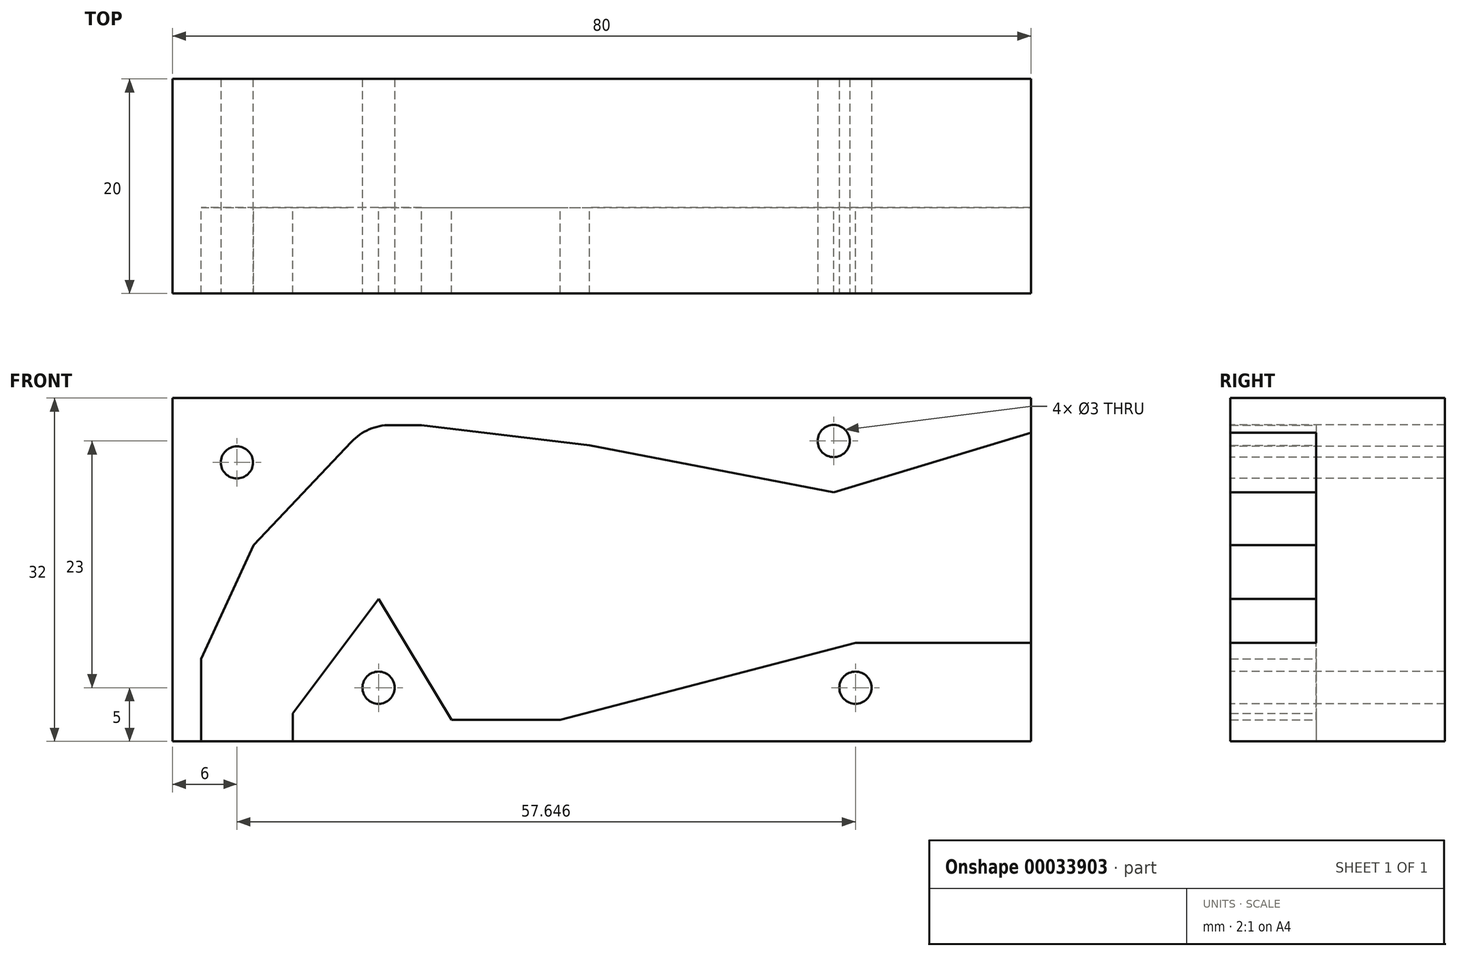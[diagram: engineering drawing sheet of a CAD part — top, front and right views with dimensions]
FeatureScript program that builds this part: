
annotation { "Feature Type Name" : "Feature", "Feature Type Description" : "" }
export const myFeature = defineFeature(function(context is Context, id is Id, definition is map)
    precondition{}
    {
        {
            var Q0;
            Q0=qCreatedBy(makeId("Front.planeOp"),FACE);
            var sketch = newSketch(context, id + "F0", { "sketchPlane" : qUnion([Q0])});
            skCircle(sketch, "E0", {"center": v(0, 0) * mm, "radius": 8 * mm});
            skLineSegment(sketch, "E1", {"start": v(0, 0) * mm, "end": v(0, 12.66) * mm});
            skArc(sketch, "E2", {"start": v(-7.6, 13.48) * mm, "mid": v(-0.91, 8.05) * mm, "end": v(6.83, 11.83) * mm});
            skLineSegment(sketch, "E3", {"start": v(0, 0) * mm, "end": v(0, -16) * mm});
            skLineSegment(sketch, "E4", {"start": v(0, 0) * mm, "end": v(8, 0) * mm});
            skPoint(sketch, "E5.endSnap0", {"position": v(0, -8) * mm});
            skLineSegment(sketch, "E6", {"start": v(-3.6, 8.53) * mm, "end": v(-19.6, -12.8) * mm});
            skLineSegment(sketch, "E7.top", {"start": v(-30, 16) * mm, "end": v(50, 16) * mm});
            skLineSegment(sketch, "E7.left", {"start": v(-30, -16) * mm, "end": v(-30, 16) * mm});
            skCircle(sketch, "E8", {"center": v(-22.8, -10.4) * mm, "radius": 4 * mm});
            skLineSegment(sketch, "E9", {"start": v(-26.25, -8.34) * mm, "end": v(-19.35, 0.86) * mm});
            skLineSegment(sketch, "E10", {"start": v(-8, 13.48) * mm, "end": v(-8, 0) * mm});
            skLineSegment(sketch, "E11", {"start": v(-8, 12.14) * mm, "end": v(-19.17, -12.08) * mm});
            skLineSegment(sketch, "E12", {"start": v(-26.43, -8.72) * mm, "end": v(-19.17, -12.08) * mm});
            skLineSegment(sketch, "E13", {"start": v(-26.43, -8.72) * mm, "end": v(-21.62, 1.72) * mm});
            skArc(sketch, "E14", {"start": v(-3.6, 8.53) * mm, "mid": v(-5.94, 9.33) * mm, "end": v(-8.3, 8.6) * mm});
            skArc(sketch, "E15.trimOffspring", {"start": v(0.36, 8) * mm, "mid": v(0.36, 8) * mm, "end": v(0.37, 8) * mm});
            skArc(sketch, "E16.trimOffspring", {"start": v(-6, 5.33) * mm, "mid": v(-5.99, 5.33) * mm, "end": v(-5.98, 5.32) * mm});
            skArc(sketch, "E17.trimOffspring", {"start": v(-7.83, 12.02) * mm, "mid": v(-10.35, 12.43) * mm, "end": v(-12.6, 11.23) * mm});
            skArc(sketch, "E18.trimOffspring", {"start": v(-8, 12.14) * mm, "mid": v(-9.1, 12.82) * mm, "end": v(-10.23, 13.45) * mm});
            skLineSegment(sketch, "E19", {"start": v(-21.62, 1.72) * mm, "end": v(-12.6, 11.23) * mm});
            skLineSegment(sketch, "E20", {"start": v(-19.35, 0.86) * mm, "end": v(-8, 8.82) * mm});
            skLineSegment(sketch, "E21.0", {"start": v(-27.34, -8.3) * mm, "end": v(-22.46, 2.29) * mm});
            skLineSegment(sketch, "E22.0", {"start": v(-22.46, 2.29) * mm, "end": v(-13.33, 11.92) * mm});
            skArc(sketch, "E23.0", {"start": v(-7.37, 12.9) * mm, "mid": v(-7.37, 12.9) * mm, "end": v(-7.38, 12.91) * mm});
            skLineSegment(sketch, "E24", {"start": v(-8, 13.48) * mm, "end": v(-9.7, 13.48) * mm});
            skArc(sketch, "E25.trimOffspring", {"start": v(-9.7, 13.48) * mm, "mid": v(-11.67, 13.08) * mm, "end": v(-13.33, 11.92) * mm});
            skLineSegment(sketch, "E26", {"start": v(-27.34, -8.3) * mm, "end": v(-27.34, -16) * mm});
            skLineSegment(sketch, "E27.0", {"start": v(-7.92, 1.1) * mm, "end": v(-8, 1) * mm});
            skLineSegment(sketch, "E28", {"start": v(-18.8, -13.4) * mm, "end": v(-18.8, -16) * mm});
            skLineSegment(sketch, "E29", {"start": v(-2.8, 8.5) * mm, "end": v(-2.8, 8.55) * mm});
            skLineSegment(sketch, "E30", {"start": v(-6.8, 13.48) * mm, "end": v(-8, 13.48) * mm});
            skLineSegment(sketch, "E31", {"start": v(0, 0) * mm, "end": v(32, 0) * mm});
            skCircle(sketch, "E32", {"center": v(32, 0) * mm, "radius": 6 * mm});
            skLineSegment(sketch, "E33", {"start": v(50, 16) * mm, "end": v(50, -16) * mm});
            skLineSegment(sketch, "E34", {"start": v(-30, -16) * mm, "end": v(50, -16) * mm});
            skLineSegment(sketch, "E35", {"start": v(8, 11.69) * mm, "end": v(8, 0) * mm});
            skArc(sketch, "E36", {"start": v(0, 8) * mm, "mid": v(-0.98, 0) * mm, "end": v(0, -8) * mm});
            skArc(sketch, "E37.0", {"start": v(0, -9) * mm, "mid": v(6.36, -6.36) * mm, "end": v(9, 0) * mm});
            skArc(sketch, "E38.trimOffspring", {"start": v(-2.8, 8.55) * mm, "mid": v(-2.83, 8.54) * mm, "end": v(-2.87, 8.53) * mm});
            skLineSegment(sketch, "E39", {"start": v(9, 0) * mm, "end": v(30.16, 5.71) * mm});
            skLineSegment(sketch, "E40", {"start": v(0, -9) * mm, "end": v(-4, -9) * mm});
            skLineSegment(sketch, "E41", {"start": v(-4, -9) * mm, "end": v(-4, -13) * mm});
            skLineSegment(sketch, "E42", {"start": v(-4, -13) * mm, "end": v(6, -13) * mm});
            skLineSegment(sketch, "E43", {"start": v(6, -13) * mm, "end": v(33.52, -5.8) * mm});
            skLineSegment(sketch, "E44", {"start": v(8.83, 11.59) * mm, "end": v(32, 0) * mm});
            skLineSegment(sketch, "E45", {"start": v(33.52, -5.8) * mm, "end": v(92.24, -5.8) * mm});
            skLineSegment(sketch, "E46", {"start": v(92.41, -3.6) * mm, "end": v(32.95, 5.92) * mm});
            skLineSegment(sketch, "E47", {"start": v(33.52, -5.8) * mm, "end": v(88.71, 21.12) * mm});
            skArc(sketch, "E48.trimOffspring", {"start": v(92.24, -5.8) * mm, "mid": v(92.34, -4.7) * mm, "end": v(92.41, -3.6) * mm});
            skLineSegment(sketch, "E49", {"start": v(32.95, 5.92) * mm, "end": v(92.41, -3.6) * mm});
            skLineSegment(sketch, "E50", {"start": v(87.88, 23.24) * mm, "end": v(30.26, 5.74) * mm});
            skArc(sketch, "E51.trimOffspring", {"start": v(88.71, 21.12) * mm, "mid": v(88.3, 22.18) * mm, "end": v(87.88, 23.24) * mm});
            skLineSegment(sketch, "E52", {"start": v(33.13, 5.9) * mm, "end": v(8, 10.73) * mm});
            skLineSegment(sketch, "E53.0", {"start": v(50, 12.78) * mm, "end": v(31.62, 7.2) * mm});
            skLineSegment(sketch, "E54.0", {"start": v(31.62, 7.2) * mm, "end": v(8.86, 11.58) * mm});
            skLineSegment(sketch, "E55.0", {"start": v(-4, -14) * mm, "end": v(6.13, -14) * mm});
            skLineSegment(sketch, "E56.0", {"start": v(6.13, -14) * mm, "end": v(33.65, -6.8) * mm});
            skLineSegment(sketch, "E57.0", {"start": v(33.65, -6.8) * mm, "end": v(50, -6.8) * mm});
            skLineSegment(sketch, "E58", {"start": v(-6.8, 13.48) * mm, "end": v(8.86, 11.58) * mm});
            skLineSegment(sketch, "E59", {"start": v(-10.8, -2.73) * mm, "end": v(-4, -14) * mm});
            skPoint(sketch, "E60.orphan", {"position": v(-2.8, 7.93) * mm});
            skLineSegment(sketch, "E61.trimOffspring", {"start": v(-10.8, -2.73) * mm, "end": v(-18.8, -13.4) * mm});
            skArc(sketch, "E62.trimOffspring", {"start": v(8, 16) * mm, "mid": v(0, 24) * mm, "end": v(-8, 16) * mm});
            skSolve(sketch);
        }
        {
            var Q0;
            {var subQ8=sQuery(id+"F0.wireOp",EDGE,"E7.left");Q0=makeQuery(id+"F0.imprint","IMPRINT",FACE,{"disambiguationData":[TD([[makeQuery(id+"F0.imprint","IMPRINT",EDGE,{"derivedFrom":subQ8}),-1.0]])]});}
            var Q1;
            {var subQ5=sQuery(id+"F0.wireOp",EDGE,"E28");Q1=makeQuery(id+"F0.imprint","IMPRINT",FACE,{"disambiguationData":[TD([[makeQuery(id+"F0.imprint","IMPRINT",EDGE,{"derivedFrom":subQ5}),1.0]])]});}
            var Q2;
            {var subQ1=sQuery(id+"F0.wireOp",EDGE,"E56.0");Q2=makeQuery(id+"F0.imprint","IMPRINT",FACE,{"disambiguationData":[TD([[makeQuery(id+"F0.imprint","IMPRINT",EDGE,{"derivedFrom":subQ1}),-1.0]])]});}
            extrude(context, id + "F1", {"entities" : qUnion([Q0, Q1, Q2]), "depth" : 8 * mm});
        }
        {
            var Q0;
            Q0=makeQuery(id+"F1.opExtrude","CAP_FACE",FACE,{"disambiguationData":[OSD([sQuery(id+"F0.wireOp",EDGE,"E7.top"),sQuery(id+"F0.wireOp",EDGE,"E7.left"),sQuery(id+"F0.wireOp",EDGE,"E21.0"),sQuery(id+"F0.wireOp",EDGE,"E22.0"),sQuery(id+"F0.wireOp",EDGE,"E24"),sQuery(id+"F0.wireOp",EDGE,"E25.trimOffspring"),sQuery(id+"F0.wireOp",EDGE,"E26"),sQuery(id+"F0.wireOp",EDGE,"E30"),sQuery(id+"F0.wireOp",EDGE,"E33"),sQuery(id+"F0.wireOp",EDGE,"E34"),sQuery(id+"F0.wireOp",EDGE,"E53.0"),sQuery(id+"F0.wireOp",EDGE,"E54.0"),sQuery(id+"F0.wireOp",EDGE,"E58")])],"isStart":true});
            var sketch = newSketch(context, id + "F2", { "sketchPlane" : qUnion([Q0])});
            skLineSegment(sketch, "E63.0.0", {"start": v(30, 16) * mm, "end": v(-50, 16) * mm});
            skLineSegment(sketch, "E63.0.1", {"start": v(-50, 16) * mm, "end": v(-50, 12.78) * mm});
            skLineSegment(sketch, "E63.0.2", {"start": v(-50, 12.78) * mm, "end": v(-31.62, 7.2) * mm});
            skLineSegment(sketch, "E63.0.3", {"start": v(-31.62, 7.2) * mm, "end": v(-8.86, 11.58) * mm});
            skLineSegment(sketch, "E63.0.4", {"start": v(-8.86, 11.58) * mm, "end": v(6.8, 13.48) * mm});
            skLineSegment(sketch, "E63.0.5", {"start": v(6.8, 13.48) * mm, "end": v(9.7, 13.48) * mm});
            skArc(sketch, "E63.0.6", {"start": v(9.7, 13.48) * mm, "mid": v(11.67, 13.08) * mm, "end": v(13.33, 11.92) * mm});
            skLineSegment(sketch, "E63.0.7", {"start": v(13.33, 11.92) * mm, "end": v(22.46, 2.29) * mm});
            skLineSegment(sketch, "E63.0.8", {"start": v(22.46, 2.29) * mm, "end": v(27.34, -8.3) * mm});
            skLineSegment(sketch, "E63.0.9", {"start": v(27.34, -8.3) * mm, "end": v(27.34, -16) * mm});
            skLineSegment(sketch, "E63.0.10", {"start": v(27.34, -16) * mm, "end": v(30, -16) * mm});
            skLineSegment(sketch, "E63.0.11", {"start": v(30, -16) * mm, "end": v(30, 16) * mm});
            skLineSegment(sketch, "E64.0.0", {"start": v(-50, -16) * mm, "end": v(18.8, -16) * mm});
            skLineSegment(sketch, "E64.0.1", {"start": v(18.8, -16) * mm, "end": v(18.8, -13.4) * mm});
            skLineSegment(sketch, "E64.0.2", {"start": v(18.8, -13.4) * mm, "end": v(10.8, -2.73) * mm});
            skLineSegment(sketch, "E64.0.3", {"start": v(10.8, -2.73) * mm, "end": v(4, -14) * mm});
            skLineSegment(sketch, "E64.0.4", {"start": v(4, -14) * mm, "end": v(-6.13, -14) * mm});
            skLineSegment(sketch, "E64.0.5", {"start": v(-6.13, -14) * mm, "end": v(-33.65, -6.8) * mm});
            skLineSegment(sketch, "E64.0.6", {"start": v(-33.65, -6.8) * mm, "end": v(-50, -6.8) * mm});
            skLineSegment(sketch, "E64.0.7", {"start": v(-50, -6.8) * mm, "end": v(-50, -16) * mm});
            skLineSegment(sketch, "E65.bottom", {"start": v(-50, 16) * mm, "end": v(30, 16) * mm});
            skLineSegment(sketch, "E65.top", {"start": v(-50, -16) * mm, "end": v(30, -16) * mm});
            skLineSegment(sketch, "E65.left", {"start": v(-50, 16) * mm, "end": v(-50, -16) * mm});
            skLineSegment(sketch, "E65.right", {"start": v(30, 16) * mm, "end": v(30, -16) * mm});
            skSolve(sketch);
        }
        {
            var Q0;
            {var subQ5=sQuery(id+"F2.wireOp",EDGE,"E63.0.2");Q0=makeQuery(id+"F2.imprint","IMPRINT",FACE,{"disambiguationData":[TD([[makeQuery(id+"F2.imprint","IMPRINT",EDGE,{"derivedFrom":subQ5}),-1.0]])]});}
            var Q1;
            {var subQ2=sQuery(id+"F2.wireOp",EDGE,"E63.0.2");Q1=makeQuery(id+"F2.imprint","IMPRINT",FACE,{"disambiguationData":[TD([[makeQuery(id+"F2.imprint","IMPRINT",EDGE,{"derivedFrom":subQ2}),1.0]])]});}
            var Q2;
            {var subQ4=sQuery(id+"F2.wireOp",EDGE,"E64.0.1");Q2=makeQuery(id+"F2.imprint","IMPRINT",FACE,{"disambiguationData":[TD([[makeQuery(id+"F2.imprint","IMPRINT",EDGE,{"derivedFrom":subQ4}),1.0]])]});}
            extrude(context, id + "F3", {"entities" : qUnion([Q0, Q1, Q2]), "operationType" : NewBodyOperationType.ADD, "depth" : 12 * mm});
        }
        {
            var Q0;
            Q0=makeQuery(id+"F1.opExtrude","CAP_FACE",FACE,{"disambiguationData":[OSD([sQuery(id+"F0.wireOp",EDGE,"E7.top"),sQuery(id+"F0.wireOp",EDGE,"E7.left"),sQuery(id+"F0.wireOp",EDGE,"E21.0"),sQuery(id+"F0.wireOp",EDGE,"E22.0"),sQuery(id+"F0.wireOp",EDGE,"E24"),sQuery(id+"F0.wireOp",EDGE,"E25.trimOffspring"),sQuery(id+"F0.wireOp",EDGE,"E26"),sQuery(id+"F0.wireOp",EDGE,"E30"),sQuery(id+"F0.wireOp",EDGE,"E33"),sQuery(id+"F0.wireOp",EDGE,"E34"),sQuery(id+"F0.wireOp",EDGE,"E53.0"),sQuery(id+"F0.wireOp",EDGE,"E54.0"),sQuery(id+"F0.wireOp",EDGE,"E58")])],"isStart":false});
            var sketch = newSketch(context, id + "F4", { "sketchPlane" : qUnion([Q0])});
            skCircle(sketch, "E66", {"center": v(-24, 10) * mm, "radius": 1.5 * mm});
            skCircle(sketch, "E67", {"center": v(31.62, 12) * mm, "radius": 1.5 * mm});
            skCircle(sketch, "E68", {"center": v(33.65, -11) * mm, "radius": 1.5 * mm});
            skCircle(sketch, "E69", {"center": v(-10.8, -11) * mm, "radius": 1.5 * mm});
            skLineSegment(sketch, "E70.0", {"start": v(-30, 16) * mm, "end": v(50, 16) * mm});
            skLineSegment(sketch, "E71.0", {"start": v(-18.8, -16) * mm, "end": v(50, -16) * mm});
            skSolve(sketch);
        }
        {
            var Q0;
            Q0=makeQuery(id+"F4.imprint","IMPRINT",FACE,{"disambiguationData":[TD([[makeQuery(id+"F4.imprint","IMPRINT",EDGE,{"derivedFrom":sQuery(id+"F4.wireOp",EDGE,"E66")}),1.0]])]});
            var Q1;
            Q1=makeQuery(id+"F4.imprint","IMPRINT",FACE,{"disambiguationData":[TD([[makeQuery(id+"F4.imprint","IMPRINT",EDGE,{"derivedFrom":sQuery(id+"F4.wireOp",EDGE,"E69")}),1.0]])]});
            var Q2;
            Q2=makeQuery(id+"F4.imprint","IMPRINT",FACE,{"disambiguationData":[TD([[makeQuery(id+"F4.imprint","IMPRINT",EDGE,{"derivedFrom":sQuery(id+"F4.wireOp",EDGE,"E68")}),1.0]])]});
            var Q3;
            Q3=makeQuery(id+"F4.imprint","IMPRINT",FACE,{"disambiguationData":[TD([[makeQuery(id+"F4.imprint","IMPRINT",EDGE,{"derivedFrom":sQuery(id+"F4.wireOp",EDGE,"E67")}),1.0]])]});
            extrude(context, id + "F5", {"entities" : qUnion([Q0, Q1, Q2, Q3]), "operationType" : NewBodyOperationType.REMOVE, "endBound" : BoundingType.THROUGH_ALL, "oppositeDirection" : true, "depth" : 25 * mm});
        }
    });
